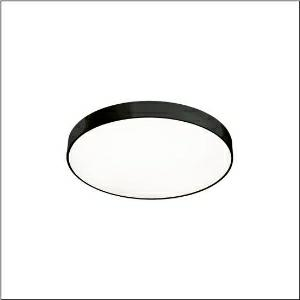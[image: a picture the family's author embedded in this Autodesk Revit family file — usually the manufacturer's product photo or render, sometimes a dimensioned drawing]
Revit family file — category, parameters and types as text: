
# Revit family: round_21_m_51mr36fm8321b
name_source: partatom
category: Lighting Fixtures
units: mm (PartAtom-declared; Revit-internal decimal feet)

## family parameters
Cut with Voids When Loaded = No
Host = Face
Light Source = No
Part Type = Normal
Room Calculation Point = No
Round Connector Dimension = Use Diameter
Shared = No

## types (1)
- --- (1 x LED, 8540 lm, 62.6 W, 3000K)
    Apparent Load = 63 VA
    CIE Flux Codes = 49 80 96 100 100
    Color Rendering = 80
    Color Temperature = 3000K
    Default Elevation = 1800 mm
    Description = Round 21 M, wall and ceiling luminaire, primary optical cover: cover, of PMMA, opal, light emission: direct distribution, primary light characteristic: symmetric, installation type: surface-mounted, suspended mounting, LED, rated luminous flux: 7.700lm, luminous efficacy: 127lm/W, light colour: 830, colour temperature: 3000K, control gear: ON/OFF Multilumen, with terminal, 3-pole, mains connection: 230V, AC, 50/60Hz, rated input power: 61W, housing, of aluminium, coated, black, diameter: 600mm, height: 62mm, protection rating (complete): IP40, insulation class (complete): insulation class I (protective earthing), certification: CE, impact resistance: IK04, permissible operating ambient temperature: -10..+35°C, packaging unit: 1 piece
    Height = 87 mm
    Lamp = 1 x LED
    Lamp Light Flux = 8540 lm
    Lamp Power = 62.6 W
    Lamp count = 1
    Length = 600 mm
    Luminous efficacy = 136 lm/W
    Manufacturer = Siteco
    ModVariant = No
    Model = 51MR36FM8321B
    Mounting Place = Ceiling
    Mounting Type = Surface mounted
    Number of Poles = 1
    OnlyDefault = Yes
    Power Factor = 1
    Product Name = Round 21 M
    Product group = wall and ceiling luminaire | ceiling mounted
    ProductGroupID = 304
    Protection Class = Protection class I
    Protection Degree = IP 40
    RLX_Detail_Level = 1
    RLX_Emergency_Light_Flux = 0 lm
    RLX_Emergency_Type = 0
    RLX_Emergency_Type_DB = No
    RlxData = <blob elided: 20405 chars, md5=60826d71>
    Socket = socket
    Standby Power = 0 W
    System Light Flux = 8540 lm
    System Power = 63 W
    Type Comments = factory setting: luminous flux: 100 % | (ON | ON | ON | ON) | 700 mA
    Type Image = l_1258332.jpg
    URL = http://relux.com
    VarID = @adj_039417
    Voltage = 0 V
    Weight = 0.00 kg
    Width = 0 mm  [stored 0 ft]

note: [stored X ft] marks values corroborated as IEEE doubles in the binary element streams (Revit-internal decimal feet)

## geometry (parser evidence)
native form markers: Blend x4, Sweep x12
no freeform markers — native parametric forms only
